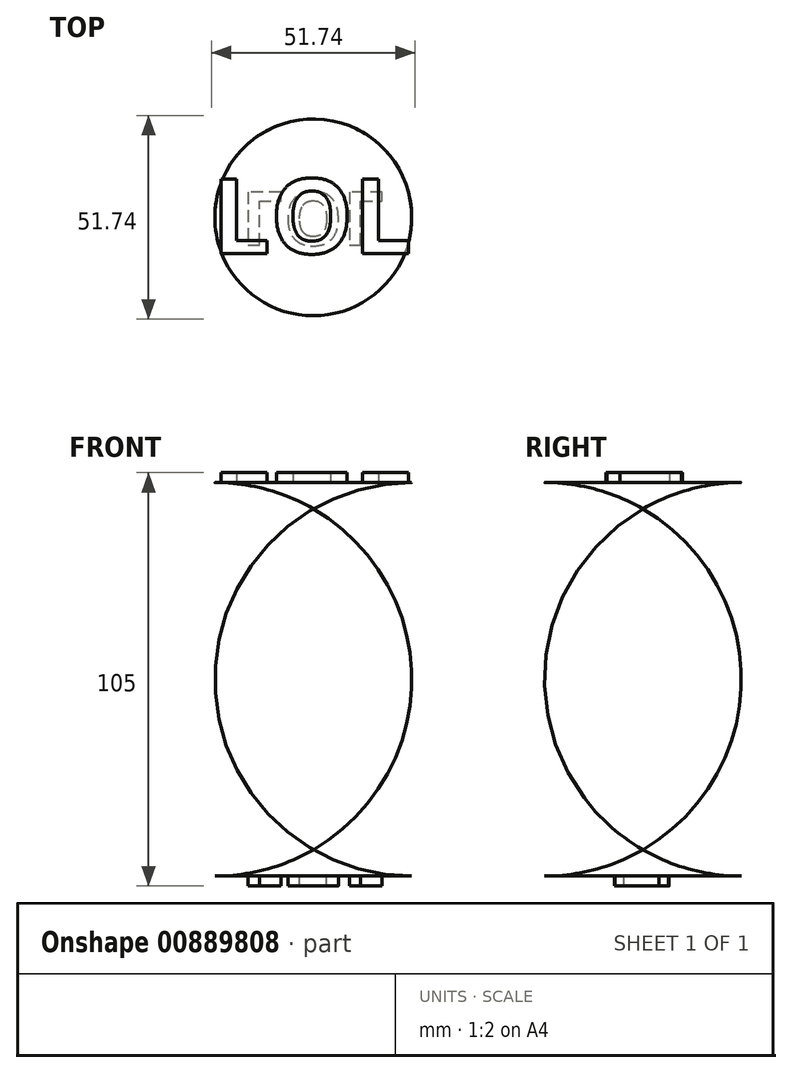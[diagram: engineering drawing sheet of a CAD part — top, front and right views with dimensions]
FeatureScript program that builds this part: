
annotation { "Feature Type Name" : "Feature", "Feature Type Description" : "" }
export const myFeature = defineFeature(function(context is Context, id is Id, definition is map)
    precondition{}
    {
        {
            var Q0;
            Q0=qCreatedBy(makeId("Top.planeOp"),FACE);
            var sketch = newSketch(context, id + "F0", { "sketchPlane" : qUnion([Q0])});
            skCircle(sketch, "E0", {"center": v(0, 0) * mm, "radius": 75 * mm});
            skSolve(sketch);
        }
        {
            var Q0;
            Q0=makeQuery(id+"F0.imprint","IMPRINT",FACE,{"disambiguationData":[TD([[makeQuery(id+"F0.imprint","IMPRINT",EDGE,{"derivedFrom":sQuery(id+"F0.wireOp",EDGE,"E0")}),1.0]])]});
            extrude(context, id + "F1", {"entities" : qUnion([Q0]), "depth" : 50 * mm, "offsetDistance" : 25 * mm});
        }
        {
            var Q0;
            Q0=makeQuery(id+"F1.opExtrude","CAP_FACE",FACE,{"disambiguationData":[OSD([sQuery(id+"F0.wireOp",EDGE,"E0")])],"isStart":true});
            extrude(context, id + "F2", {"entities" : qUnion([Q0]), "operationType" : NewBodyOperationType.ADD, "depth" : 50 * mm, "offsetDistance" : 25 * mm});
        }
        {
            var Q0;
            Q0=makeQuery(id+"F1.opExtrude","CAP_FACE",FACE,{"disambiguationData":[OSD([sQuery(id+"F0.wireOp",EDGE,"E0")])],"isStart":false});
            fillet(context, id + "F3", {"entities" : qUnion([Q0]), "radius" : 50 * mm, "tangentPropagation" : true, "allowEdgeOverflow" : false});
        }
        {
            var Q0;
            Q0=makeQuery(id+"F2.opExtrude","CAP_FACE",FACE,{"disambiguationData":[OSD([sQuery(id+"F0.wireOp",EDGE,"E0")])],"isStart":false});
            fillet(context, id + "F4", {"entities" : qUnion([Q0]), "radius" : 50 * mm, "tangentPropagation" : true, "allowEdgeOverflow" : false});
        }
        {
            var Q0;
            Q0=makeQuery(id+"F1.opExtrude","CAP_FACE",FACE,{"disambiguationData":[OSD([sQuery(id+"F0.wireOp",EDGE,"E0")])],"isStart":false});
            var sketch = newSketch(context, id + "F5", { "sketchPlane" : qUnion([Q0])});
            skText(sketch, "E1", { "text": "LOL\n", "fontName": "OpenSans-Bold.ttf"});
            const initialGuessF5  = {"E1": [-0.02586, -0.00916, 1, 0, 0.01905]};
            skSetInitialGuess(sketch, initialGuessF5);
            skSolve(sketch);
        }
        {
            var Q0;
            Q0 = qSketchRegion(id + "F5", true);
            extrude(context, id + "F6", {"entities" : qUnion([Q0]), "operationType" : NewBodyOperationType.ADD, "depth" : 2.5 * mm, "offsetDistance" : 25 * mm});
        }
        {
            var Q0;
            Q0=makeQuery(id+"F2.opExtrude","CAP_FACE",FACE,{"disambiguationData":[OSD([sQuery(id+"F0.wireOp",EDGE,"E0")])],"isStart":false});
            var sketch = newSketch(context, id + "F7", { "sketchPlane" : qUnion([Q0])});
            skText(sketch, "E2", { "text": "LOL", "fontName": "OpenSans-Bold.ttf"});
            const initialGuessF7  = {"E2": [-0.01824, -0.00644, 1, 0, 0.0136]};
            skSetInitialGuess(sketch, initialGuessF7);
            skSolve(sketch);
        }
        {
            var Q0;
            Q0 = qSketchRegion(id + "F7", true);
            extrude(context, id + "F8", {"entities" : qUnion([Q0]), "operationType" : NewBodyOperationType.ADD, "depth" : 2.5 * mm, "offsetDistance" : 25 * mm});
        }
    });
